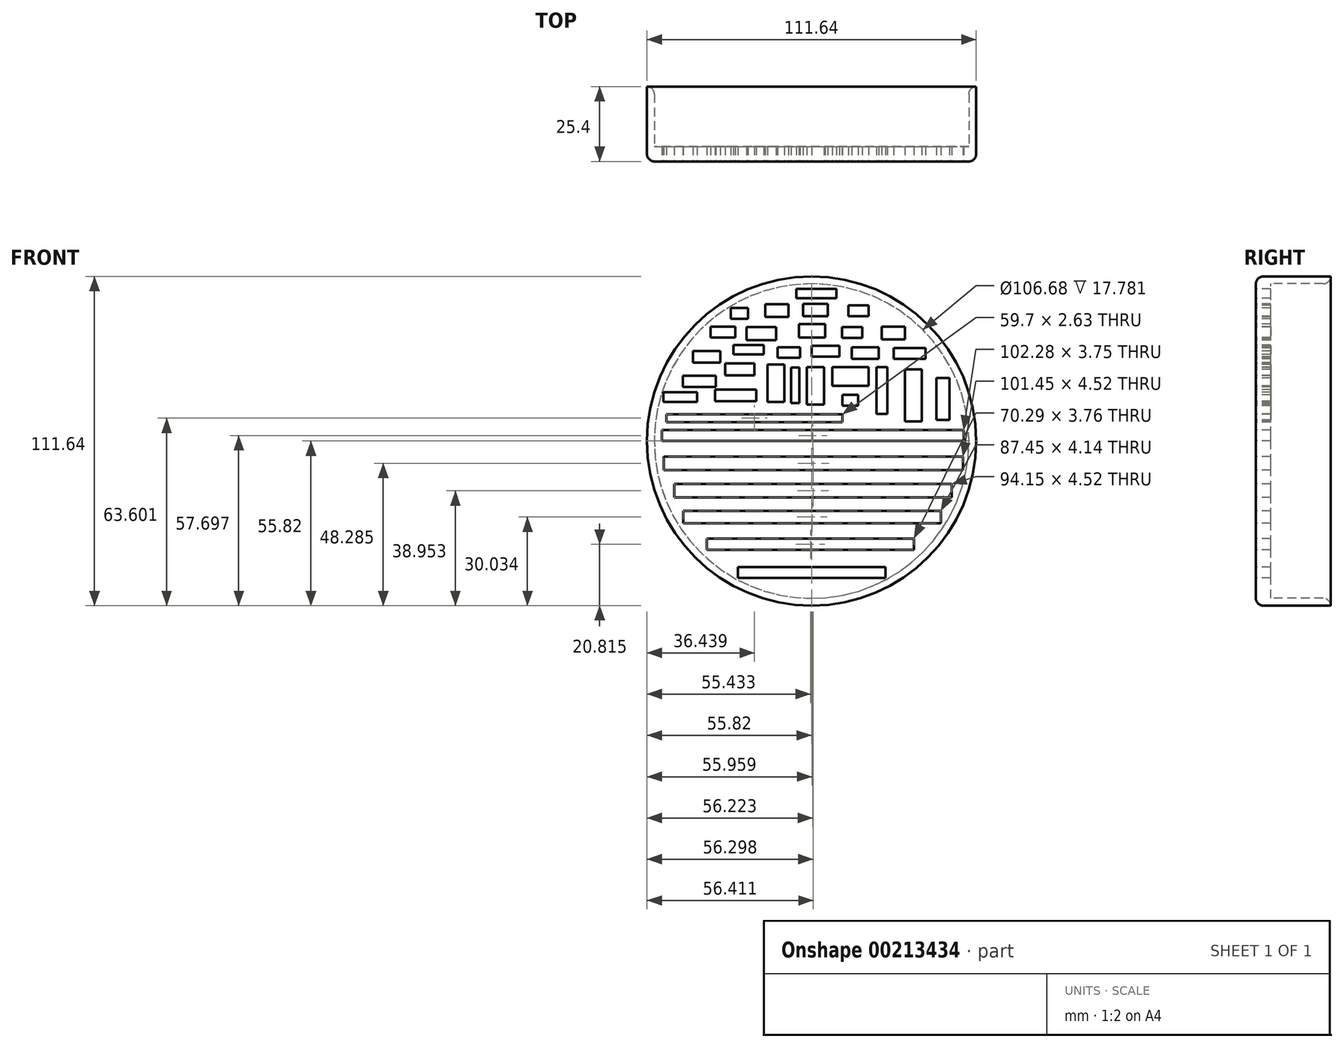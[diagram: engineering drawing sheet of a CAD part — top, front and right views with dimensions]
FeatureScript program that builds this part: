
annotation { "Feature Type Name" : "Feature", "Feature Type Description" : "" }
export const myFeature = defineFeature(function(context is Context, id is Id, definition is map)
    precondition{}
    {
        {
            var Q0;
            Q0=qCreatedBy(makeId("Front.planeOp"),FACE);
            var sketch = newSketch(context, id + "F0", { "sketchPlane" : qUnion([Q0])});
            skCircle(sketch, "E0", {"center": v(0, 0) * mm, "radius": 53.34 * mm});
            skCircle(sketch, "E1", {"center": v(0, 0) * mm, "radius": 55.82 * mm});
            skSolve(sketch);
        }
        {
            var Q0;
            Q0=makeQuery(id+"F0.imprint","IMPRINT",FACE,{"disambiguationData":[TD([[makeQuery(id+"F0.imprint","IMPRINT",EDGE,{"derivedFrom":sQuery(id+"F0.wireOp",EDGE,"E0")}),-1.0]])]});
            extrude(context, id + "F1", {"entities" : qUnion([Q0]), "oppositeDirection" : true, "depth" : 25.4 * mm});
        }
        {
            var Q0;
            Q0=makeQuery(id+"F0.imprint","IMPRINT",FACE,{"disambiguationData":[TD([[makeQuery(id+"F0.imprint","IMPRINT",EDGE,{"derivedFrom":sQuery(id+"F0.wireOp",EDGE,"E0")}),1.0]])]});
            extrude(context, id + "F2", {"entities" : qUnion([Q0]), "operationType" : NewBodyOperationType.ADD, "oppositeDirection" : true, "depth" : 5.08 * mm});
        }
        {
            var Q0;
            Q0=makeQuery(id+"F0.imprint","IMPRINT",FACE,{"disambiguationData":[TD([[makeQuery(id+"F0.imprint","IMPRINT",EDGE,{"derivedFrom":sQuery(id+"F0.wireOp",EDGE,"E0")}),1.0]])]});
            var sketch = newSketch(context, id + "F3", { "sketchPlane" : qUnion([Q0])});
            skLineSegment(sketch, "E2.bottom", {"start": v(-25.88, 38.77) * mm, "end": v(-34.3, 38.77) * mm});
            skLineSegment(sketch, "E2.top", {"start": v(-25.88, 35.07) * mm, "end": v(-34.3, 35.07) * mm});
            skLineSegment(sketch, "E2.left", {"start": v(-25.88, 38.77) * mm, "end": v(-25.88, 35.07) * mm});
            skLineSegment(sketch, "E2.right", {"start": v(-34.3, 38.77) * mm, "end": v(-34.3, 35.07) * mm});
            skPoint(sketch, "E2.middle", {"position": v(-30.09, 36.92) * mm});
            skLineSegment(sketch, "E3.bottom", {"start": v(-12, 38.6) * mm, "end": v(-22.1, 38.6) * mm});
            skLineSegment(sketch, "E3.top", {"start": v(-12, 34.23) * mm, "end": v(-22.1, 34.23) * mm});
            skLineSegment(sketch, "E3.left", {"start": v(-12, 38.6) * mm, "end": v(-12, 34.23) * mm});
            skLineSegment(sketch, "E3.right", {"start": v(-22.1, 38.6) * mm, "end": v(-22.1, 34.23) * mm});
            skPoint(sketch, "E3.middle", {"position": v(-17.05, 36.42) * mm});
            skLineSegment(sketch, "E4.bottom", {"start": v(-4.27, 35.07) * mm, "end": v(4.56, 35.07) * mm});
            skLineSegment(sketch, "E4.top", {"start": v(-4.27, 39.7) * mm, "end": v(4.56, 39.7) * mm});
            skLineSegment(sketch, "E4.left", {"start": v(-4.27, 35.07) * mm, "end": v(-4.27, 39.7) * mm});
            skLineSegment(sketch, "E4.right", {"start": v(4.56, 35.07) * mm, "end": v(4.56, 39.7) * mm});
            skLineSegment(sketch, "E5.bottom", {"start": v(-15.7, 42.14) * mm, "end": v(-7.8, 42.14) * mm});
            skLineSegment(sketch, "E5.top", {"start": v(-15.7, 46.43) * mm, "end": v(-7.8, 46.43) * mm});
            skLineSegment(sketch, "E5.left", {"start": v(-15.7, 42.14) * mm, "end": v(-15.7, 46.43) * mm});
            skLineSegment(sketch, "E5.right", {"start": v(-7.8, 42.14) * mm, "end": v(-7.8, 46.43) * mm});
            skLineSegment(sketch, "E6.bottom", {"start": v(-2.88, 42.34) * mm, "end": v(5.52, 42.34) * mm});
            skLineSegment(sketch, "E6.top", {"start": v(-2.88, 46.5) * mm, "end": v(5.52, 46.5) * mm});
            skLineSegment(sketch, "E6.left", {"start": v(-2.88, 42.34) * mm, "end": v(-2.88, 46.5) * mm});
            skLineSegment(sketch, "E6.right", {"start": v(5.52, 42.34) * mm, "end": v(5.52, 46.5) * mm});
            skLineSegment(sketch, "E7.bottom", {"start": v(-27.4, 41.43) * mm, "end": v(-21.6, 41.43) * mm});
            skLineSegment(sketch, "E7.top", {"start": v(-27.4, 45.12) * mm, "end": v(-21.6, 45.12) * mm});
            skLineSegment(sketch, "E7.left", {"start": v(-27.4, 41.43) * mm, "end": v(-27.4, 45.12) * mm});
            skLineSegment(sketch, "E7.right", {"start": v(-21.6, 41.43) * mm, "end": v(-21.6, 45.12) * mm});
            skLineSegment(sketch, "E8.bottom", {"start": v(12.46, 42.4) * mm, "end": v(19.35, 42.4) * mm});
            skLineSegment(sketch, "E8.top", {"start": v(12.46, 46.08) * mm, "end": v(19.35, 46.08) * mm});
            skLineSegment(sketch, "E8.left", {"start": v(12.46, 42.4) * mm, "end": v(12.46, 46.08) * mm});
            skLineSegment(sketch, "E8.right", {"start": v(19.35, 42.4) * mm, "end": v(19.35, 46.08) * mm});
            skLineSegment(sketch, "E9.bottom", {"start": v(10.27, 35.01) * mm, "end": v(17.14, 35.01) * mm});
            skLineSegment(sketch, "E9.top", {"start": v(10.27, 38.62) * mm, "end": v(17.14, 38.62) * mm});
            skLineSegment(sketch, "E9.left", {"start": v(10.27, 35.01) * mm, "end": v(10.27, 38.62) * mm});
            skLineSegment(sketch, "E9.right", {"start": v(17.14, 35.01) * mm, "end": v(17.14, 38.62) * mm});
            skLineSegment(sketch, "E10.bottom", {"start": v(23.77, 34.52) * mm, "end": v(31.68, 34.52) * mm});
            skLineSegment(sketch, "E10.top", {"start": v(23.77, 38.77) * mm, "end": v(31.68, 38.77) * mm});
            skLineSegment(sketch, "E10.left", {"start": v(23.77, 34.52) * mm, "end": v(23.77, 38.77) * mm});
            skLineSegment(sketch, "E10.right", {"start": v(31.68, 34.52) * mm, "end": v(31.68, 38.77) * mm});
            skLineSegment(sketch, "E11.bottom", {"start": v(-11.5, 28.3) * mm, "end": v(-3.84, 28.3) * mm});
            skLineSegment(sketch, "E11.top", {"start": v(-11.5, 31.84) * mm, "end": v(-3.84, 31.84) * mm});
            skLineSegment(sketch, "E11.left", {"start": v(-11.5, 28.3) * mm, "end": v(-11.5, 31.84) * mm});
            skLineSegment(sketch, "E11.right", {"start": v(-3.84, 28.3) * mm, "end": v(-3.84, 31.84) * mm});
            skLineSegment(sketch, "E12.bottom", {"start": v(-29.36, 22.26) * mm, "end": v(-19.4, 22.26) * mm});
            skLineSegment(sketch, "E12.top", {"start": v(-29.36, 26.29) * mm, "end": v(-19.4, 26.29) * mm});
            skLineSegment(sketch, "E12.left", {"start": v(-29.36, 22.26) * mm, "end": v(-29.36, 26.29) * mm});
            skLineSegment(sketch, "E12.right", {"start": v(-19.4, 22.26) * mm, "end": v(-19.4, 26.29) * mm});
            skLineSegment(sketch, "E13.bottom", {"start": v(-26.49, 29.4) * mm, "end": v(-16.24, 29.4) * mm});
            skLineSegment(sketch, "E13.top", {"start": v(-26.49, 32.51) * mm, "end": v(-16.24, 32.51) * mm});
            skLineSegment(sketch, "E13.left", {"start": v(-26.49, 29.4) * mm, "end": v(-26.49, 32.51) * mm});
            skLineSegment(sketch, "E13.right", {"start": v(-16.24, 29.4) * mm, "end": v(-16.24, 32.51) * mm});
            skLineSegment(sketch, "E14.bottom", {"start": v(-40.23, 26.57) * mm, "end": v(-30.9, 26.57) * mm});
            skLineSegment(sketch, "E14.top", {"start": v(-40.23, 30.5) * mm, "end": v(-30.9, 30.5) * mm});
            skLineSegment(sketch, "E14.left", {"start": v(-40.23, 26.57) * mm, "end": v(-40.23, 30.5) * mm});
            skLineSegment(sketch, "E14.right", {"start": v(-30.9, 26.57) * mm, "end": v(-30.9, 30.5) * mm});
            skLineSegment(sketch, "E15.bottom", {"start": v(-43.68, 18.39) * mm, "end": v(-32.43, 18.39) * mm});
            skLineSegment(sketch, "E15.top", {"start": v(-43.68, 22.22) * mm, "end": v(-32.43, 22.22) * mm});
            skLineSegment(sketch, "E15.left", {"start": v(-43.68, 18.39) * mm, "end": v(-43.68, 22.22) * mm});
            skLineSegment(sketch, "E15.right", {"start": v(-32.43, 18.39) * mm, "end": v(-32.43, 22.22) * mm});
            skLineSegment(sketch, "E16.bottom", {"start": v(-50.24, 13.22) * mm, "end": v(-38.84, 13.22) * mm});
            skLineSegment(sketch, "E16.top", {"start": v(-50.24, 16.62) * mm, "end": v(-38.84, 16.62) * mm});
            skLineSegment(sketch, "E16.left", {"start": v(-50.24, 13.22) * mm, "end": v(-50.24, 16.62) * mm});
            skLineSegment(sketch, "E16.right", {"start": v(-38.84, 13.22) * mm, "end": v(-38.84, 16.62) * mm});
            skLineSegment(sketch, "E17.bottom", {"start": v(-32.71, 13.5) * mm, "end": v(-18.73, 13.5) * mm});
            skLineSegment(sketch, "E17.top", {"start": v(-32.71, 17.48) * mm, "end": v(-18.73, 17.48) * mm});
            skLineSegment(sketch, "E17.left", {"start": v(-32.71, 13.5) * mm, "end": v(-32.71, 17.48) * mm});
            skLineSegment(sketch, "E17.right", {"start": v(-18.73, 13.5) * mm, "end": v(-18.73, 17.48) * mm});
            skLineSegment(sketch, "E18.bottom", {"start": v(-14.9, 26) * mm, "end": v(-9.25, 26) * mm});
            skLineSegment(sketch, "E18.top", {"start": v(-14.9, 13.26) * mm, "end": v(-9.25, 13.26) * mm});
            skLineSegment(sketch, "E18.left", {"start": v(-14.9, 26) * mm, "end": v(-14.9, 13.26) * mm});
            skLineSegment(sketch, "E18.right", {"start": v(-9.25, 26) * mm, "end": v(-9.25, 13.26) * mm});
            skLineSegment(sketch, "E19.bottom", {"start": v(-1.64, 25.14) * mm, "end": v(4.25, 25.14) * mm});
            skLineSegment(sketch, "E19.top", {"start": v(-1.64, 12.35) * mm, "end": v(4.25, 12.35) * mm});
            skLineSegment(sketch, "E19.left", {"start": v(-1.64, 25.14) * mm, "end": v(-1.64, 12.35) * mm});
            skLineSegment(sketch, "E19.right", {"start": v(4.25, 25.14) * mm, "end": v(4.25, 12.35) * mm});
            skLineSegment(sketch, "E20.bottom", {"start": v(-6.96, 12.83) * mm, "end": v(-4.18, 12.83) * mm});
            skLineSegment(sketch, "E20.top", {"start": v(-6.96, 24.95) * mm, "end": v(-4.18, 24.95) * mm});
            skLineSegment(sketch, "E20.left", {"start": v(-6.96, 12.83) * mm, "end": v(-6.96, 24.95) * mm});
            skLineSegment(sketch, "E20.right", {"start": v(-4.18, 12.83) * mm, "end": v(-4.18, 24.95) * mm});
            skLineSegment(sketch, "E21.bottom", {"start": v(0, 32.37) * mm, "end": v(9.42, 32.37) * mm});
            skLineSegment(sketch, "E21.top", {"start": v(0, 28.58) * mm, "end": v(9.42, 28.58) * mm});
            skLineSegment(sketch, "E21.left", {"start": v(0, 32.37) * mm, "end": v(0, 28.58) * mm});
            skLineSegment(sketch, "E21.right", {"start": v(9.42, 32.37) * mm, "end": v(9.42, 28.58) * mm});
            skLineSegment(sketch, "E22.bottom", {"start": v(13.58, 27.91) * mm, "end": v(22.73, 27.91) * mm});
            skLineSegment(sketch, "E22.top", {"start": v(13.58, 31.74) * mm, "end": v(22.73, 31.74) * mm});
            skLineSegment(sketch, "E22.left", {"start": v(13.58, 27.91) * mm, "end": v(13.58, 31.74) * mm});
            skLineSegment(sketch, "E22.right", {"start": v(22.73, 27.91) * mm, "end": v(22.73, 31.74) * mm});
            skLineSegment(sketch, "E23.bottom", {"start": v(27.9, 27.82) * mm, "end": v(38.67, 27.82) * mm});
            skLineSegment(sketch, "E23.top", {"start": v(27.9, 31.6) * mm, "end": v(38.67, 31.6) * mm});
            skLineSegment(sketch, "E23.left", {"start": v(27.9, 27.82) * mm, "end": v(27.9, 31.6) * mm});
            skLineSegment(sketch, "E23.right", {"start": v(38.67, 27.82) * mm, "end": v(38.67, 31.6) * mm});
            skLineSegment(sketch, "E24.bottom", {"start": v(-5.14, 48.45) * mm, "end": v(8.41, 48.45) * mm});
            skLineSegment(sketch, "E24.top", {"start": v(-5.14, 51.56) * mm, "end": v(8.41, 51.56) * mm});
            skLineSegment(sketch, "E24.left", {"start": v(-5.14, 48.45) * mm, "end": v(-5.14, 51.56) * mm});
            skLineSegment(sketch, "E24.right", {"start": v(8.41, 48.45) * mm, "end": v(8.41, 51.56) * mm});
            skLineSegment(sketch, "E25.bottom", {"start": v(10.47, 12.02) * mm, "end": v(15.74, 12.02) * mm});
            skLineSegment(sketch, "E25.top", {"start": v(10.47, 15.66) * mm, "end": v(15.74, 15.66) * mm});
            skLineSegment(sketch, "E25.left", {"start": v(10.47, 12.02) * mm, "end": v(10.47, 15.66) * mm});
            skLineSegment(sketch, "E25.right", {"start": v(15.74, 12.02) * mm, "end": v(15.74, 15.66) * mm});
            skLineSegment(sketch, "E26.bottom", {"start": v(7.02, 18.77) * mm, "end": v(19.38, 18.77) * mm});
            skLineSegment(sketch, "E26.top", {"start": v(7.02, 25.09) * mm, "end": v(19.38, 25.09) * mm});
            skLineSegment(sketch, "E26.left", {"start": v(7.02, 18.77) * mm, "end": v(7.02, 25.09) * mm});
            skLineSegment(sketch, "E26.right", {"start": v(19.38, 18.77) * mm, "end": v(19.38, 25.09) * mm});
            skLineSegment(sketch, "E27.bottom", {"start": v(-25, -46.37) * mm, "end": v(25.05, -46.37) * mm});
            skLineSegment(sketch, "E27.top", {"start": v(-25, -42.68) * mm, "end": v(25.05, -42.68) * mm});
            skLineSegment(sketch, "E27.left", {"start": v(-25, -46.37) * mm, "end": v(-25, -42.68) * mm});
            skLineSegment(sketch, "E27.right", {"start": v(25.05, -46.37) * mm, "end": v(25.05, -42.68) * mm});
            skLineSegment(sketch, "E28.bottom", {"start": v(-35.53, -36.89) * mm, "end": v(34.76, -36.89) * mm});
            skLineSegment(sketch, "E28.top", {"start": v(-35.53, -33.12) * mm, "end": v(34.76, -33.12) * mm});
            skLineSegment(sketch, "E28.left", {"start": v(-35.53, -36.89) * mm, "end": v(-35.53, -33.12) * mm});
            skLineSegment(sketch, "E28.right", {"start": v(34.76, -36.89) * mm, "end": v(34.76, -33.12) * mm});
            skLineSegment(sketch, "E29.bottom", {"start": v(-43.59, -27.86) * mm, "end": v(43.87, -27.86) * mm});
            skLineSegment(sketch, "E29.top", {"start": v(-43.59, -23.72) * mm, "end": v(43.87, -23.72) * mm});
            skLineSegment(sketch, "E29.left", {"start": v(-43.59, -27.86) * mm, "end": v(-43.59, -23.72) * mm});
            skLineSegment(sketch, "E29.right", {"start": v(43.87, -27.86) * mm, "end": v(43.87, -23.72) * mm});
            skLineSegment(sketch, "E30.bottom", {"start": v(-46.6, -19.13) * mm, "end": v(47.55, -19.13) * mm});
            skLineSegment(sketch, "E30.top", {"start": v(-46.6, -14.6) * mm, "end": v(47.55, -14.6) * mm});
            skLineSegment(sketch, "E30.left", {"start": v(-46.6, -19.13) * mm, "end": v(-46.6, -14.6) * mm});
            skLineSegment(sketch, "E30.right", {"start": v(47.55, -19.13) * mm, "end": v(47.55, -14.6) * mm});
            skLineSegment(sketch, "E31.bottom", {"start": v(-50.14, -9.8) * mm, "end": v(51.32, -9.8) * mm});
            skLineSegment(sketch, "E31.top", {"start": v(-50.14, -5.28) * mm, "end": v(51.32, -5.28) * mm});
            skLineSegment(sketch, "E31.left", {"start": v(-50.14, -9.8) * mm, "end": v(-50.14, -5.28) * mm});
            skLineSegment(sketch, "E31.right", {"start": v(51.32, -9.8) * mm, "end": v(51.32, -5.28) * mm});
            skLineSegment(sketch, "E32.bottom", {"start": v(-50.74, 0) * mm, "end": v(51.54, 0) * mm});
            skLineSegment(sketch, "E32.top", {"start": v(-50.74, 3.75) * mm, "end": v(51.54, 3.75) * mm});
            skLineSegment(sketch, "E32.left", {"start": v(-50.74, 0) * mm, "end": v(-50.74, 3.75) * mm});
            skLineSegment(sketch, "E32.right", {"start": v(51.54, 0) * mm, "end": v(51.54, 3.75) * mm});
            skLineSegment(sketch, "E33.bottom", {"start": v(21.97, 9.25) * mm, "end": v(25.65, 9.25) * mm});
            skLineSegment(sketch, "E33.top", {"start": v(21.97, 25.13) * mm, "end": v(25.65, 25.13) * mm});
            skLineSegment(sketch, "E33.left", {"start": v(21.97, 9.25) * mm, "end": v(21.97, 25.13) * mm});
            skLineSegment(sketch, "E33.right", {"start": v(25.65, 9.25) * mm, "end": v(25.65, 25.13) * mm});
            skLineSegment(sketch, "E34.bottom", {"start": v(31.6, 24.3) * mm, "end": v(37.32, 24.3) * mm});
            skLineSegment(sketch, "E34.top", {"start": v(31.6, 6.61) * mm, "end": v(37.32, 6.61) * mm});
            skLineSegment(sketch, "E34.left", {"start": v(31.6, 24.3) * mm, "end": v(31.6, 6.61) * mm});
            skLineSegment(sketch, "E34.right", {"start": v(37.32, 24.3) * mm, "end": v(37.32, 6.61) * mm});
            skLineSegment(sketch, "E35.bottom", {"start": v(42.36, 21.37) * mm, "end": v(46.73, 21.37) * mm});
            skLineSegment(sketch, "E35.top", {"start": v(42.36, 7.14) * mm, "end": v(46.73, 7.14) * mm});
            skLineSegment(sketch, "E35.left", {"start": v(42.36, 21.37) * mm, "end": v(42.36, 7.14) * mm});
            skLineSegment(sketch, "E35.right", {"start": v(46.73, 21.37) * mm, "end": v(46.73, 7.14) * mm});
            skLineSegment(sketch, "E36.bottom", {"start": v(-49.23, 6.46) * mm, "end": v(10.47, 6.46) * mm});
            skLineSegment(sketch, "E36.top", {"start": v(-49.23, 9.1) * mm, "end": v(10.47, 9.1) * mm});
            skLineSegment(sketch, "E36.left", {"start": v(-49.23, 6.46) * mm, "end": v(-49.23, 9.1) * mm});
            skLineSegment(sketch, "E36.right", {"start": v(10.47, 6.46) * mm, "end": v(10.47, 9.1) * mm});
            skLineSegment(sketch, "E37.bottom", {"start": v(15.64, 7.67) * mm, "end": v(27.08, 7.67) * mm});
            skLineSegment(sketch, "E37.top", {"start": v(15.64, 6.24) * mm, "end": v(27.08, 6.24) * mm});
            skLineSegment(sketch, "E37.left", {"start": v(15.64, 7.67) * mm, "end": v(15.64, 6.24) * mm});
            skLineSegment(sketch, "E37.right", {"start": v(27.08, 7.67) * mm, "end": v(27.08, 6.24) * mm});
            skSolve(sketch);
        }
        {
            var Q0;
            Q0=makeQuery(id+"F3.imprint","IMPRINT",FACE,{"disambiguationData":[TD([[makeQuery(id+"F3.imprint","IMPRINT",EDGE,{"derivedFrom":sQuery(id+"F3.wireOp",EDGE,"E24.bottom")}),1.0]])]});
            var Q1;
            Q1=makeQuery(id+"F3.imprint","IMPRINT",FACE,{"disambiguationData":[TD([[makeQuery(id+"F3.imprint","IMPRINT",EDGE,{"derivedFrom":sQuery(id+"F3.wireOp",EDGE,"E6.bottom")}),1.0]])]});
            var Q2;
            Q2=makeQuery(id+"F3.imprint","IMPRINT",FACE,{"disambiguationData":[TD([[makeQuery(id+"F3.imprint","IMPRINT",EDGE,{"derivedFrom":sQuery(id+"F3.wireOp",EDGE,"E5.bottom")}),1.0]])]});
            var Q3;
            Q3=makeQuery(id+"F3.imprint","IMPRINT",FACE,{"disambiguationData":[TD([[makeQuery(id+"F3.imprint","IMPRINT",EDGE,{"derivedFrom":sQuery(id+"F3.wireOp",EDGE,"E7.bottom")}),1.0]])]});
            var Q4;
            Q4=makeQuery(id+"F3.imprint","IMPRINT",FACE,{"disambiguationData":[TD([[makeQuery(id+"F3.imprint","IMPRINT",EDGE,{"derivedFrom":sQuery(id+"F3.wireOp",EDGE,"E2.bottom")}),1.0]])]});
            var Q5;
            Q5=makeQuery(id+"F3.imprint","IMPRINT",FACE,{"disambiguationData":[TD([[makeQuery(id+"F3.imprint","IMPRINT",EDGE,{"derivedFrom":sQuery(id+"F3.wireOp",EDGE,"E3.bottom")}),1.0]])]});
            var Q6;
            Q6=makeQuery(id+"F3.imprint","IMPRINT",FACE,{"disambiguationData":[TD([[makeQuery(id+"F3.imprint","IMPRINT",EDGE,{"derivedFrom":sQuery(id+"F3.wireOp",EDGE,"E4.bottom")}),1.0]])]});
            var Q7;
            Q7=makeQuery(id+"F3.imprint","IMPRINT",FACE,{"disambiguationData":[TD([[makeQuery(id+"F3.imprint","IMPRINT",EDGE,{"derivedFrom":sQuery(id+"F3.wireOp",EDGE,"E9.bottom")}),1.0]])]});
            var Q8;
            Q8=makeQuery(id+"F3.imprint","IMPRINT",FACE,{"disambiguationData":[TD([[makeQuery(id+"F3.imprint","IMPRINT",EDGE,{"derivedFrom":sQuery(id+"F3.wireOp",EDGE,"E8.bottom")}),1.0]])]});
            var Q9;
            Q9=makeQuery(id+"F3.imprint","IMPRINT",FACE,{"disambiguationData":[TD([[makeQuery(id+"F3.imprint","IMPRINT",EDGE,{"derivedFrom":sQuery(id+"F3.wireOp",EDGE,"E10.bottom")}),1.0]])]});
            var Q10;
            Q10=makeQuery(id+"F3.imprint","IMPRINT",FACE,{"disambiguationData":[TD([[makeQuery(id+"F3.imprint","IMPRINT",EDGE,{"derivedFrom":sQuery(id+"F3.wireOp",EDGE,"E13.bottom")}),1.0]])]});
            var Q11;
            Q11=makeQuery(id+"F3.imprint","IMPRINT",FACE,{"disambiguationData":[TD([[makeQuery(id+"F3.imprint","IMPRINT",EDGE,{"derivedFrom":sQuery(id+"F3.wireOp",EDGE,"E14.bottom")}),1.0]])]});
            var Q12;
            Q12=makeQuery(id+"F3.imprint","IMPRINT",FACE,{"disambiguationData":[TD([[makeQuery(id+"F3.imprint","IMPRINT",EDGE,{"derivedFrom":sQuery(id+"F3.wireOp",EDGE,"E12.bottom")}),1.0]])]});
            var Q13;
            Q13=makeQuery(id+"F3.imprint","IMPRINT",FACE,{"disambiguationData":[TD([[makeQuery(id+"F3.imprint","IMPRINT",EDGE,{"derivedFrom":sQuery(id+"F3.wireOp",EDGE,"E17.bottom")}),1.0]])]});
            var Q14;
            Q14=makeQuery(id+"F3.imprint","IMPRINT",FACE,{"disambiguationData":[TD([[makeQuery(id+"F3.imprint","IMPRINT",EDGE,{"derivedFrom":sQuery(id+"F3.wireOp",EDGE,"E15.bottom")}),1.0]])]});
            var Q15;
            Q15=makeQuery(id+"F3.imprint","IMPRINT",FACE,{"disambiguationData":[TD([[makeQuery(id+"F3.imprint","IMPRINT",EDGE,{"derivedFrom":sQuery(id+"F3.wireOp",EDGE,"E16.bottom")}),1.0]])]});
            var Q16;
            Q16=makeQuery(id+"F3.imprint","IMPRINT",FACE,{"disambiguationData":[TD([[makeQuery(id+"F3.imprint","IMPRINT",EDGE,{"derivedFrom":sQuery(id+"F3.wireOp",EDGE,"E11.bottom")}),1.0]])]});
            var Q17;
            Q17=makeQuery(id+"F3.imprint","IMPRINT",FACE,{"disambiguationData":[TD([[makeQuery(id+"F3.imprint","IMPRINT",EDGE,{"derivedFrom":sQuery(id+"F3.wireOp",EDGE,"E21.bottom")}),-1.0]])]});
            var Q18;
            Q18=makeQuery(id+"F3.imprint","IMPRINT",FACE,{"disambiguationData":[TD([[makeQuery(id+"F3.imprint","IMPRINT",EDGE,{"derivedFrom":sQuery(id+"F3.wireOp",EDGE,"E22.bottom")}),1.0]])]});
            var Q19;
            Q19=makeQuery(id+"F3.imprint","IMPRINT",FACE,{"disambiguationData":[TD([[makeQuery(id+"F3.imprint","IMPRINT",EDGE,{"derivedFrom":sQuery(id+"F3.wireOp",EDGE,"E23.bottom")}),1.0]])]});
            var Q20;
            Q20=makeQuery(id+"F3.imprint","IMPRINT",FACE,{"disambiguationData":[TD([[makeQuery(id+"F3.imprint","IMPRINT",EDGE,{"derivedFrom":sQuery(id+"F3.wireOp",EDGE,"E18.bottom")}),-1.0]])]});
            var Q21;
            Q21=makeQuery(id+"F3.imprint","IMPRINT",FACE,{"disambiguationData":[TD([[makeQuery(id+"F3.imprint","IMPRINT",EDGE,{"derivedFrom":sQuery(id+"F3.wireOp",EDGE,"E20.bottom")}),1.0]])]});
            var Q22;
            Q22=makeQuery(id+"F3.imprint","IMPRINT",FACE,{"disambiguationData":[TD([[makeQuery(id+"F3.imprint","IMPRINT",EDGE,{"derivedFrom":sQuery(id+"F3.wireOp",EDGE,"E19.bottom")}),-1.0]])]});
            var Q23;
            Q23=makeQuery(id+"F3.imprint","IMPRINT",FACE,{"disambiguationData":[TD([[makeQuery(id+"F3.imprint","IMPRINT",EDGE,{"derivedFrom":sQuery(id+"F3.wireOp",EDGE,"E26.bottom")}),1.0]])]});
            var Q24;
            Q24=makeQuery(id+"F3.imprint","IMPRINT",FACE,{"disambiguationData":[TD([[makeQuery(id+"F3.imprint","IMPRINT",EDGE,{"derivedFrom":sQuery(id+"F3.wireOp",EDGE,"E25.bottom")}),1.0]])]});
            var Q25;
            Q25=makeQuery(id+"F3.imprint","IMPRINT",FACE,{"disambiguationData":[TD([[makeQuery(id+"F3.imprint","IMPRINT",EDGE,{"derivedFrom":sQuery(id+"F3.wireOp",EDGE,"E33.bottom")}),1.0]])]});
            var Q26;
            Q26=makeQuery(id+"F3.imprint","IMPRINT",FACE,{"disambiguationData":[TD([[makeQuery(id+"F3.imprint","IMPRINT",EDGE,{"derivedFrom":sQuery(id+"F3.wireOp",EDGE,"E34.bottom")}),-1.0]])]});
            var Q27;
            Q27=makeQuery(id+"F3.imprint","IMPRINT",FACE,{"disambiguationData":[TD([[makeQuery(id+"F3.imprint","IMPRINT",EDGE,{"derivedFrom":sQuery(id+"F3.wireOp",EDGE,"E35.bottom")}),-1.0]])]});
            var Q28;
            Q28=makeQuery(id+"F3.imprint","IMPRINT",FACE,{"disambiguationData":[TD([[makeQuery(id+"F3.imprint","IMPRINT",EDGE,{"derivedFrom":sQuery(id+"F3.wireOp",EDGE,"E36.bottom")}),1.0]])]});
            var Q29;
            Q29=makeQuery(id+"F3.imprint","IMPRINT",FACE,{"disambiguationData":[TD([[makeQuery(id+"F3.imprint","IMPRINT",EDGE,{"derivedFrom":sQuery(id+"F3.wireOp",EDGE,"E32.bottom")}),1.0]])]});
            var Q30;
            Q30=makeQuery(id+"F3.imprint","IMPRINT",FACE,{"disambiguationData":[TD([[makeQuery(id+"F3.imprint","IMPRINT",EDGE,{"derivedFrom":sQuery(id+"F3.wireOp",EDGE,"E31.bottom")}),1.0]])]});
            var Q31;
            Q31=makeQuery(id+"F3.imprint","IMPRINT",FACE,{"disambiguationData":[TD([[makeQuery(id+"F3.imprint","IMPRINT",EDGE,{"derivedFrom":sQuery(id+"F3.wireOp",EDGE,"E27.bottom")}),1.0]])]});
            var Q32;
            Q32=makeQuery(id+"F3.imprint","IMPRINT",FACE,{"disambiguationData":[TD([[makeQuery(id+"F3.imprint","IMPRINT",EDGE,{"derivedFrom":sQuery(id+"F3.wireOp",EDGE,"E28.bottom")}),1.0]])]});
            var Q33;
            Q33=makeQuery(id+"F3.imprint","IMPRINT",FACE,{"disambiguationData":[TD([[makeQuery(id+"F3.imprint","IMPRINT",EDGE,{"derivedFrom":sQuery(id+"F3.wireOp",EDGE,"E29.bottom")}),1.0]])]});
            var Q34;
            Q34=makeQuery(id+"F3.imprint","IMPRINT",FACE,{"disambiguationData":[TD([[makeQuery(id+"F3.imprint","IMPRINT",EDGE,{"derivedFrom":sQuery(id+"F3.wireOp",EDGE,"E30.bottom")}),1.0]])]});
            extrude(context, id + "F4", {"entities" : qUnion([Q0, Q1, Q2, Q3, Q4, Q5, Q6, Q7, Q8, Q9, Q10, Q11, Q12, Q13, Q14, Q15, Q16, Q17, Q18, Q19, Q20, Q21, Q22, Q23, Q24, Q25, Q26, Q27, Q28, Q29, Q30, Q31, Q32, Q33, Q34]), "operationType" : NewBodyOperationType.REMOVE, "oppositeDirection" : true, "depth" : 25.4 * mm});
        }
        {
            var Q0;
            Q0=makeQuery(id+"F1.opExtrude","CAP_EDGE",EDGE,{"disambiguationData":[OSD([sQuery(id+"F0.wireOp",EDGE,"E1")])],"isStart":true});
            var Q1;
            Q1=makeQuery(id+"F1.opExtrude","CAP_EDGE",EDGE,{"disambiguationData":[OSD([sQuery(id+"F0.wireOp",EDGE,"E0")])],"isStart":false});
            fillet(context, id + "F5", {"entities" : qUnion([Q0, Q1]), "radius" : 2.54 * mm, "tangentPropagation" : true, "allowEdgeOverflow" : false});
        }
    });
